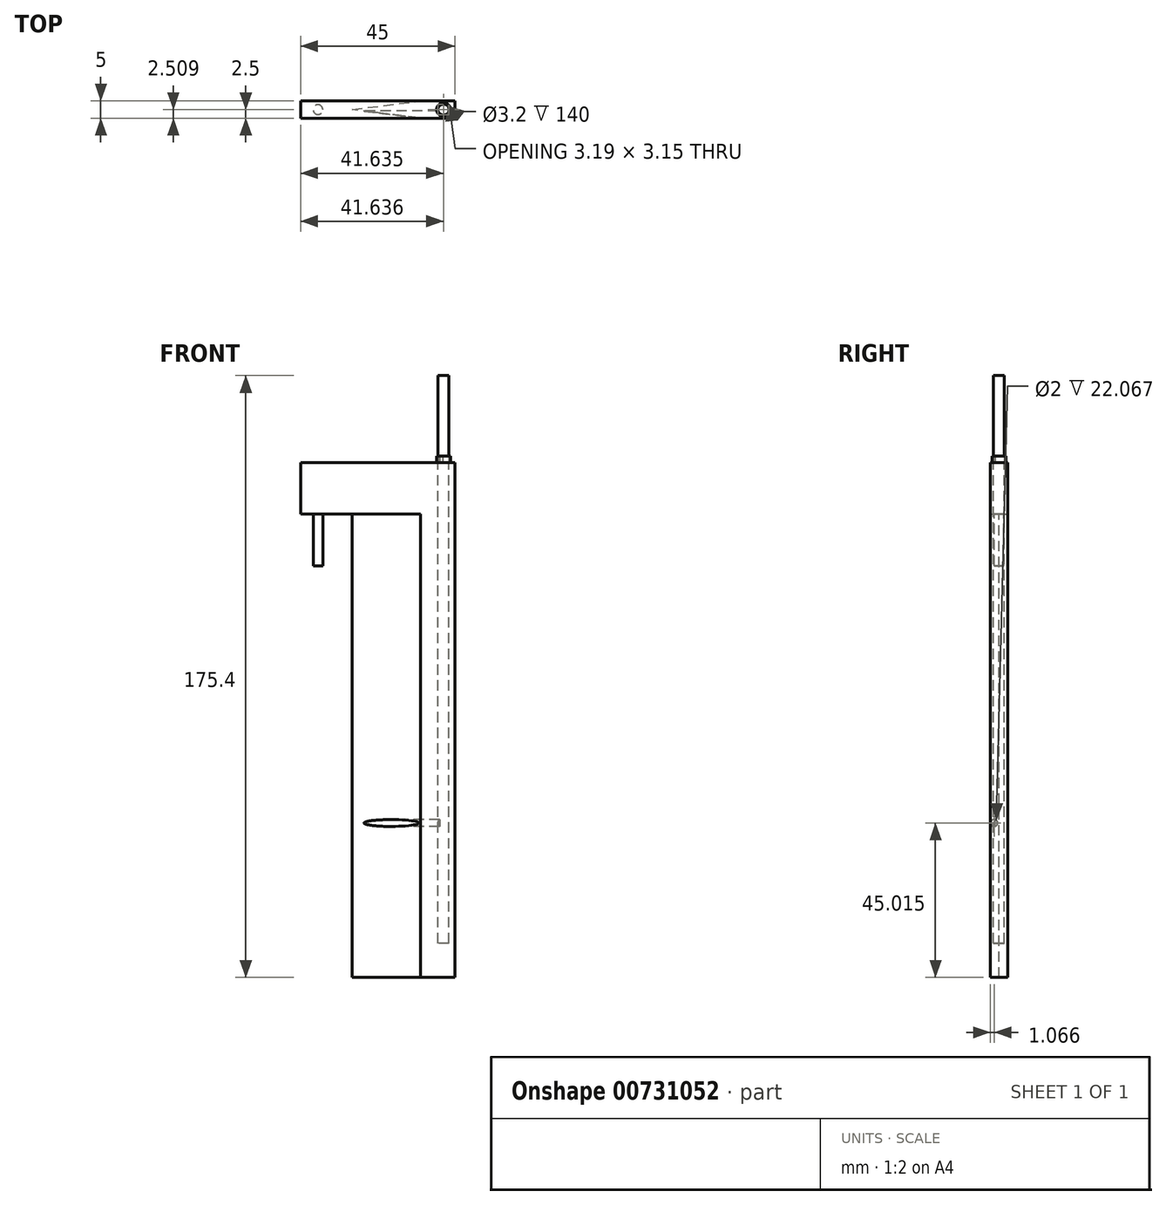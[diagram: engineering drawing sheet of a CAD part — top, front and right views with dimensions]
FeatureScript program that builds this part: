
annotation { "Feature Type Name" : "Feature", "Feature Type Description" : "" }
export const myFeature = defineFeature(function(context is Context, id is Id, definition is map)
    precondition{}
    {
        {
            var Q0;
            Q0=qCreatedBy(makeId("Front.planeOp"),FACE);
            var sketch = newSketch(context, id + "F0", { "sketchPlane" : qUnion([Q0])});
            skLineSegment(sketch, "E0.bottom", {"start": v(0, 0) * mm, "end": v(30, 0) * mm});
            skLineSegment(sketch, "E0.top", {"start": v(0, -150) * mm, "end": v(30, -150) * mm});
            skLineSegment(sketch, "E0.left", {"start": v(0, 0) * mm, "end": v(0, -150) * mm});
            skLineSegment(sketch, "E0.right", {"start": v(30, 0) * mm, "end": v(30, -150) * mm});
            skSolve(sketch);
        }
        {
            var Q0;
            Q0=makeQuery(id+"F0.imprint","IMPRINT",FACE,{"disambiguationData":[TD([[makeQuery(id+"F0.imprint","IMPRINT",EDGE,{"derivedFrom":sQuery(id+"F0.wireOp",EDGE,"E0.bottom")}),-1.0]])]});
            extrude(context, id + "F1", {"entities" : qUnion([Q0]), "depth" : 5 * mm, "offsetDistance" : 25.4 * mm});
        }
        {
            var Q0;
            Q0=makeQuery(id+"F1.opExtrude","SWEPT_FACE",FACE,{"disambiguationData":[OSD([sQuery(id+"F0.wireOp",EDGE,"E0.bottom")])]});
            var sketch = newSketch(context, id + "F2", { "sketchPlane" : qUnion([Q0])});
            skLineSegment(sketch, "E1", {"start": v(19.93, 0) * mm, "end": v(0, -2.5) * mm});
            skLineSegment(sketch, "E2", {"start": v(0, -2.5) * mm, "end": v(19.93, -5) * mm});
            skCircle(sketch, "E3", {"center": v(26.64, -2.5) * mm, "radius": 1.6 * mm});
            skPoint(sketch, "E3.centerSnap0", {"position": v(30, -2.5) * mm});
            skSolve(sketch);
        }
        {
            var Q0;
            {var subQ0=sQuery(id+"F2.wireOp",EDGE,"E1");Q0=makeQuery(id+"F2.imprint","IMPRINT",FACE,{"disambiguationData":[TD([[makeQuery(id+"F2.imprint","IMPRINT",EDGE,{"derivedFrom":subQ0}),-1.0]])]});}
            var Q1;
            {var subQ0=sQuery(id+"F2.wireOp",EDGE,"E2");Q1=makeQuery(id+"F2.imprint","IMPRINT",FACE,{"disambiguationData":[TD([[makeQuery(id+"F2.imprint","IMPRINT",EDGE,{"derivedFrom":subQ0}),-1.0]])]});}
            extrude(context, id + "F3", {"entities" : qUnion([Q0, Q1]), "operationType" : NewBodyOperationType.REMOVE, "endBound" : BoundingType.THROUGH_ALL, "oppositeDirection" : true, "depth" : 25.4 * mm, "offsetDistance" : 25.4 * mm});
        }
        {
            var Q0;
            Q0=qSketchRegion(id+"F2",true);
            extrude(context, id + "F4", {"entities" : qUnion([Q0]), "operationType" : NewBodyOperationType.REMOVE, "oppositeDirection" : true, "depth" : 140 * mm, "offsetDistance" : 25.4 * mm});
        }
        {
            var Q0;
            Q0=qCreatedBy(makeId("Right.planeOp"),FACE);
            var sketch = newSketch(context, id + "F5", { "sketchPlane" : qUnion([Q0])});
            skLineSegment(sketch, "E4", {"start": v(0, -150.04) * mm, "end": v(0, -104.98) * mm});
            skLineSegment(sketch, "E5", {"start": v(-5.25, -150.04) * mm, "end": v(0, -150.04) * mm});
            skCircle(sketch, "E6", {"center": v(-3.93, -104.98) * mm, "radius": 1 * mm});
            skPoint(sketch, "E7.start.orphan", {"position": v(-2.62, -150.04) * mm});
            skPoint(sketch, "E8.end.orphan", {"position": v(-2.62, -104.98) * mm});
            skPoint(sketch, "E9.start.orphan", {"position": v(-5.25, -104.98) * mm});
            skSolve(sketch);
        }
        {
            var Q0;
            Q0=makeQuery(id+"F5.imprint","IMPRINT",FACE,{"disambiguationData":[TD([[makeQuery(id+"F5.imprint","IMPRINT",EDGE,{"derivedFrom":sQuery(id+"F5.wireOp",EDGE,"E6")}),1.0]])]});
            extrude(context, id + "F6", {"entities" : qUnion([Q0]), "operationType" : NewBodyOperationType.REMOVE, "depth" : 25.52 * mm, "offsetDistance" : 25.4 * mm});
        }
        {
            var Q0;
            {var subQ0=sQuery(id+"F2.wireOp",EDGE,"E1");Q0=makeQuery(id+"F2.imprint","IMPRINT",FACE,{"disambiguationData":[TD([[makeQuery(id+"F2.imprint","IMPRINT",EDGE,{"derivedFrom":subQ0}),-1.0]])]});}
            var Q1;
            {var subQ3=sQuery(id+"F2.wireOp",EDGE,"E1");Q1=makeQuery(id+"F2.imprint","IMPRINT",FACE,{"disambiguationData":[TD([[makeQuery(id+"F2.imprint","IMPRINT",EDGE,{"derivedFrom":subQ3}),1.0]])]});}
            var Q2;
            {var subQ0=sQuery(id+"F2.wireOp",EDGE,"E2");Q2=makeQuery(id+"F2.imprint","IMPRINT",FACE,{"disambiguationData":[TD([[makeQuery(id+"F2.imprint","IMPRINT",EDGE,{"derivedFrom":subQ0}),-1.0]])]});}
            extrude(context, id + "F7", {"entities" : qUnion([Q0, Q1, Q2]), "operationType" : NewBodyOperationType.ADD, "oppositeDirection" : true, "depth" : 15 * mm, "offsetDistance" : 25.4 * mm});
        }
        {
            var Q0;
            Q0=makeQuery(id+"F7.opExtrude","SWEPT_FACE",FACE,{"disambiguationData":[OSD([sQuery(id+"F0.wireOp",EDGE,"E0.bottom"),sQuery(id+"F0.wireOp",EDGE,"E0.left")])]});
            var sketch = newSketch(context, id + "F8", { "sketchPlane" : qUnion([Q0])});
            skLineSegment(sketch, "E10.bottom", {"start": v(0, 0) * mm, "end": v(5, 0) * mm});
            skLineSegment(sketch, "E10.top", {"start": v(0, -15) * mm, "end": v(5, -15) * mm});
            skLineSegment(sketch, "E10.left", {"start": v(0, 0) * mm, "end": v(0, -15) * mm});
            skLineSegment(sketch, "E10.right", {"start": v(5, 0) * mm, "end": v(5, -15) * mm});
            skSolve(sketch);
        }
        {
            var Q0;
            Q0=makeQuery(id+"F8.imprint","IMPRINT",FACE,{"disambiguationData":[TD([[makeQuery(id+"F8.imprint","IMPRINT",EDGE,{"derivedFrom":sQuery(id+"F8.wireOp",EDGE,"E10.bottom")}),1.0]])]});
            extrude(context, id + "F9", {"entities" : qUnion([Q0]), "operationType" : NewBodyOperationType.ADD, "depth" : 15 * mm, "offsetDistance" : 25.4 * mm});
        }
        {
            var Q0;
            {var subQ0=sQuery(id+"F0.wireOp",EDGE,"E0.bottom");Q0=makeQuery(id+"F9.boolean.opBoolean","MERGE",FACE,{"derivedFrom":[makeQuery(id+"F7.boolean.opBoolean","MERGE",FACE,{"derivedFrom":[makeQuery(id+"F1.opExtrude","SWEPT_FACE",FACE,{"disambiguationData":[OSD([subQ0])]}),makeQuery(id+"F7.opExtrude","CAP_FACE",FACE,{"disambiguationData":[OSD([subQ0,sQuery(id+"F0.wireOp",EDGE,"E0.left"),sQuery(id+"F0.wireOp",EDGE,"E0.right"),sQuery(id+"F2.wireOp",EDGE,"E3")])],"isStart":true})]}),makeQuery(id+"F9.opExtrude","SWEPT_FACE",FACE,{"disambiguationData":[OSD([sQuery(id+"F8.wireOp",EDGE,"E10.bottom")])]})]});}
            var sketch = newSketch(context, id + "F10", { "sketchPlane" : qUnion([Q0])});
            skCircle(sketch, "E11", {"center": v(-9.96, -2.5) * mm, "radius": 1.4 * mm});
            skPoint(sketch, "E11.centerSnap0", {"position": v(-15, -2.5) * mm});
            skSolve(sketch);
        }
        {
            var Q0;
            Q0=makeQuery(id+"F10.imprint","IMPRINT",FACE,{"disambiguationData":[TD([[makeQuery(id+"F10.imprint","IMPRINT",EDGE,{"derivedFrom":sQuery(id+"F10.wireOp",EDGE,"E11")}),1.0]])]});
            extrude(context, id + "F11", {"entities" : qUnion([Q0]), "operationType" : NewBodyOperationType.ADD, "oppositeDirection" : true, "depth" : 30 * mm, "offsetDistance" : 25.4 * mm});
        }
        {
            var Q0;
            Q0=makeQuery(id+"F2.imprint","IMPRINT",FACE,{"disambiguationData":[TD([[makeQuery(id+"F2.imprint","IMPRINT",EDGE,{"derivedFrom":sQuery(id+"F2.wireOp",EDGE,"E3")}),1.0]])]});
            var sketch = newSketch(context, id + "F12", { "sketchPlane" : qUnion([Q0])});
            skCircle(sketch, "E12", {"center": v(26.66, -2.5) * mm, "radius": 2.04 * mm});
            skCircle(sketch, "E13", {"center": v(26.66, -2.5) * mm, "radius": 1.6 * mm});
            skSolve(sketch);
        }
        {
            var Q0;
            Q0=makeQuery(id+"F2.imprint","IMPRINT",FACE,{"disambiguationData":[TD([[makeQuery(id+"F2.imprint","IMPRINT",EDGE,{"derivedFrom":sQuery(id+"F2.wireOp",EDGE,"E3")}),1.0]])]});
            extrude(context, id + "F13", {"entities" : qUnion([Q0]), "depth" : 25.4 * mm, "offsetDistance" : 25.4 * mm});
        }
        {
            var Q0;
            Q0=makeQuery(id+"F12.imprint","IMPRINT",FACE,{"disambiguationData":[TD([[makeQuery(id+"F12.imprint","IMPRINT",EDGE,{"derivedFrom":sQuery(id+"F12.wireOp",EDGE,"E12")}),1.0]])]});
            var Q1;
            Q1=sQuery(id+"F12.wireOp",EDGE,"E12");
            extrude(context, id + "F14", {"entities" : qUnion([Q0]), "surfaceEntities" : qUnion([Q1]), "depth" : 2 * mm, "offsetDistance" : 25.4 * mm});
        }
    });
